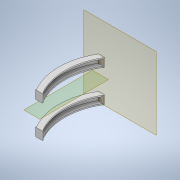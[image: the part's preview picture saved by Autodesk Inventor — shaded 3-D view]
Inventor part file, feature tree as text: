
AUTODESK INVENTOR PART (.ipt)
format: ipt  version: 2021 (Build 250183000, 183)  size: 167,424 bytes
history: native  units: mm
features: sketch x3, plane x2, mirror x2, sweep x1, extrude x1, projected_geometry x1
ambient origin geometry x8: Origin, YZ Plane, XZ Plane, XY Plane, X Axis, Y Axis, Z Axis, Center Point
bodies: Solid1 (feature_tree)
feature tree (10):
  sketch  "Sketch1"  dims[d0=100.0mm d1=7.0mm]
  plane  "Work Plane1"
  sweep  "Sweep1"
  extrude  "Extrusion1"  Depth=1.0mm
  mirror  "Mirror1"
  plane  "Work Plane2"
  mirror  "Mirror2"
  sketch  "Sketch2"  dims[d2=9.0mm d3=1.0mm]
  sketch  "Sketch3"  dims[d4=9.0mm d5=1.0mm d14=0.0mm d15=0.0mm d16=0.5mm d17=1.0mm d18=0.0mm d19=10.0mm]
  projected_geometry  "Projected Loop1"
